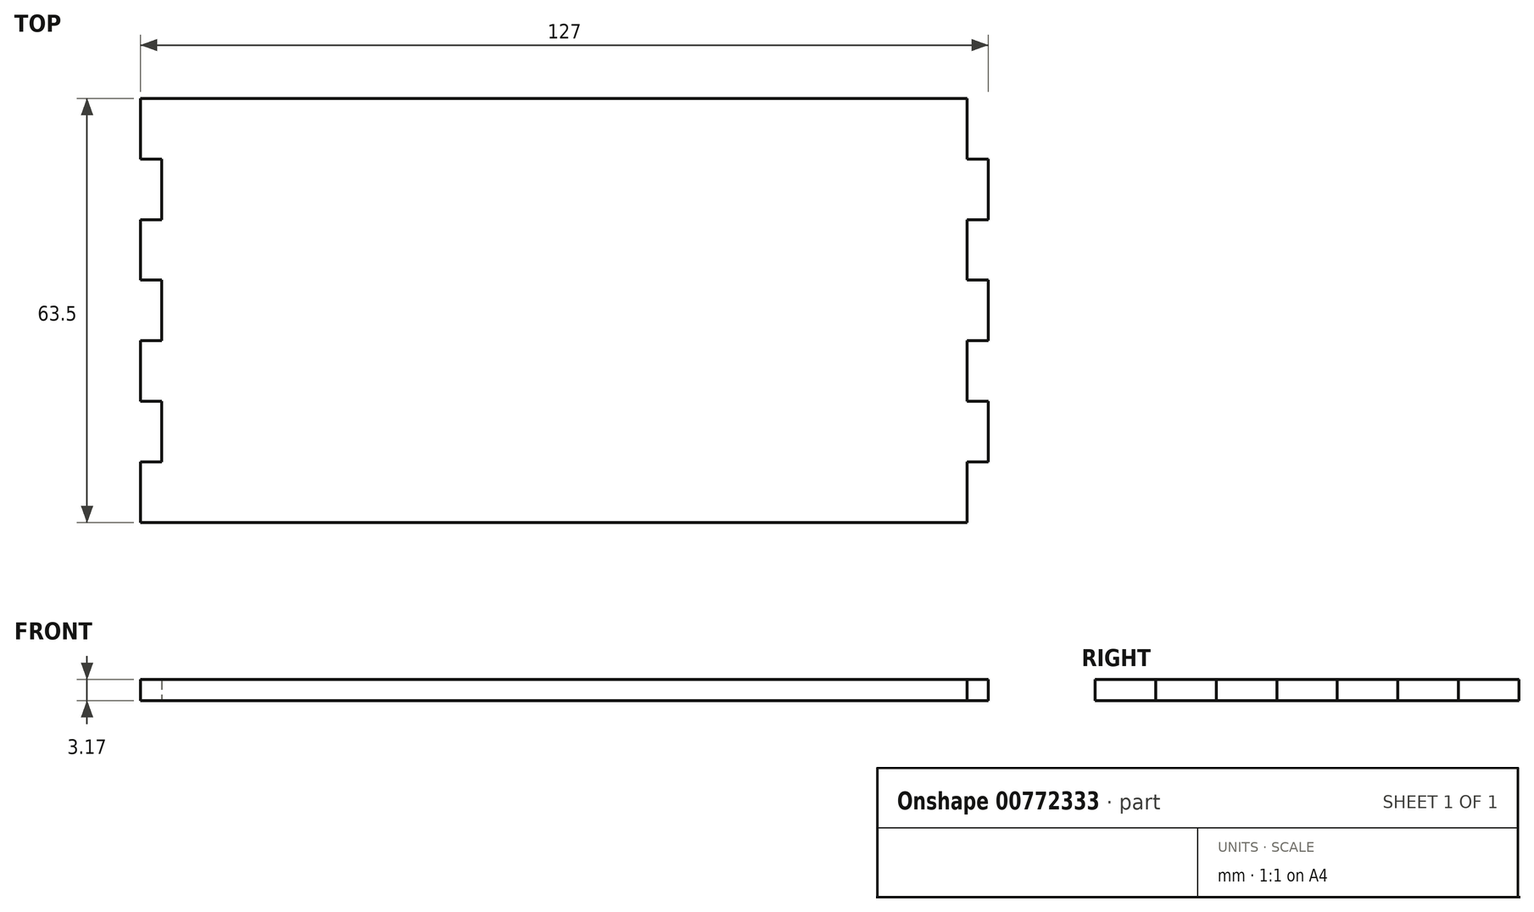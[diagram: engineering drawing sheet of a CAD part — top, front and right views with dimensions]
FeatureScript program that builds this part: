
annotation { "Feature Type Name" : "Feature", "Feature Type Description" : "" }
export const myFeature = defineFeature(function(context is Context, id is Id, definition is map)
    precondition{}
    {
        {
            var Q0;
            Q0=qCreatedBy(makeId("Top.planeOp"),FACE);
            var sketch = newSketch(context, id + "F0", { "sketchPlane" : qUnion([Q0])});
            skLineSegment(sketch, "E0.bottom", {"start": v(0, 0) * mm, "end": v(123.83, 0) * mm});
            skLineSegment(sketch, "E0.top", {"start": v(0, 63.5) * mm, "end": v(123.83, 63.5) * mm});
            skLineSegment(sketch, "E0.left", {"start": v(0, 0) * mm, "end": v(0, 9.07) * mm});
            skLineSegment(sketch, "E0.right", {"start": v(127, 9.07) * mm, "end": v(127, 18.14) * mm});
            skPoint(sketch, "E1", {"position": v(0, 9.07) * mm});
            skPoint(sketch, "E2", {"position": v(0, 18.14) * mm});
            skPoint(sketch, "E3", {"position": v(0, 36.29) * mm});
            skPoint(sketch, "E4", {"position": v(0, 45.36) * mm});
            skPoint(sketch, "E5", {"position": v(3.18, 0) * mm});
            skPoint(sketch, "E6", {"position": v(123.83, 0) * mm});
            skLineSegment(sketch, "E7", {"start": v(3.18, 9.07) * mm, "end": v(3.18, 18.14) * mm});
            skLineSegment(sketch, "E8", {"start": v(123.83, 0) * mm, "end": v(123.83, 9.07) * mm});
            skPoint(sketch, "E9", {"position": v(0, 54.43) * mm});
            skPoint(sketch, "E10", {"position": v(127, 54.43) * mm});
            skPoint(sketch, "E11", {"position": v(127, 45.36) * mm});
            skPoint(sketch, "E12", {"position": v(127, 36.29) * mm});
            skPoint(sketch, "E13", {"position": v(0, 27.21) * mm});
            skPoint(sketch, "E14", {"position": v(127, 27.21) * mm});
            skPoint(sketch, "E15", {"position": v(127, 18.14) * mm});
            skPoint(sketch, "E16", {"position": v(127, 9.07) * mm});
            skLineSegment(sketch, "E17", {"start": v(0, 54.43) * mm, "end": v(3.17, 54.43) * mm});
            skLineSegment(sketch, "E18", {"start": v(0, 45.36) * mm, "end": v(3.17, 45.36) * mm});
            skLineSegment(sketch, "E19", {"start": v(0, 36.29) * mm, "end": v(3.17, 36.29) * mm});
            skLineSegment(sketch, "E20", {"start": v(0, 27.21) * mm, "end": v(3.17, 27.21) * mm});
            skLineSegment(sketch, "E21", {"start": v(0, 18.14) * mm, "end": v(3.18, 18.14) * mm});
            skLineSegment(sketch, "E22", {"start": v(0, 9.07) * mm, "end": v(3.18, 9.07) * mm});
            skLineSegment(sketch, "E23", {"start": v(127, 54.43) * mm, "end": v(123.83, 54.43) * mm});
            skLineSegment(sketch, "E24", {"start": v(127, 45.36) * mm, "end": v(123.83, 45.36) * mm});
            skLineSegment(sketch, "E25", {"start": v(127, 36.29) * mm, "end": v(123.83, 36.29) * mm});
            skLineSegment(sketch, "E26", {"start": v(127, 18.14) * mm, "end": v(123.83, 18.14) * mm});
            skLineSegment(sketch, "E27", {"start": v(127, 9.07) * mm, "end": v(123.83, 9.07) * mm});
            skLineSegment(sketch, "E28", {"start": v(127, 27.21) * mm, "end": v(123.83, 27.21) * mm});
            skPoint(sketch, "E29.orphan", {"position": v(3.17, 63.5) * mm});
            skLineSegment(sketch, "E30.trimOffspring", {"start": v(0, 54.43) * mm, "end": v(0, 63.5) * mm});
            skLineSegment(sketch, "E31.trimOffspring", {"start": v(3.17, 45.36) * mm, "end": v(3.17, 54.43) * mm});
            skLineSegment(sketch, "E32.trimOffspring", {"start": v(0, 36.29) * mm, "end": v(0, 45.36) * mm});
            skLineSegment(sketch, "E33.trimOffspring", {"start": v(3.17, 27.21) * mm, "end": v(3.17, 36.29) * mm});
            skLineSegment(sketch, "E34.trimOffspring", {"start": v(0, 18.14) * mm, "end": v(0, 27.21) * mm});
            skLineSegment(sketch, "E35.trimOffspring", {"start": v(123.83, 54.43) * mm, "end": v(123.83, 63.5) * mm});
            skLineSegment(sketch, "E36.trimOffspring", {"start": v(127, 45.36) * mm, "end": v(127, 54.43) * mm});
            skLineSegment(sketch, "E37.trimOffspring", {"start": v(123.83, 36.29) * mm, "end": v(123.83, 45.36) * mm});
            skLineSegment(sketch, "E38.trimOffspring", {"start": v(127, 27.21) * mm, "end": v(127, 36.29) * mm});
            skLineSegment(sketch, "E39.trimOffspring", {"start": v(123.83, 18.14) * mm, "end": v(123.83, 27.21) * mm});
            skPoint(sketch, "E40.orphan", {"position": v(127, 0) * mm});
            skSolve(sketch);
        }
        {
            var Q0;
            Q0=makeQuery(id+"F0.imprint","IMPRINT",FACE,{"disambiguationData":[TD([[makeQuery(id+"F0.imprint","IMPRINT",EDGE,{"derivedFrom":sQuery(id+"F0.wireOp",EDGE,"E0.bottom")}),1.0]])]});
            extrude(context, id + "F1", {"entities" : qUnion([Q0]), "depth" : 3.17 * mm, "offsetDistance" : 25.4 * mm});
        }
    });
